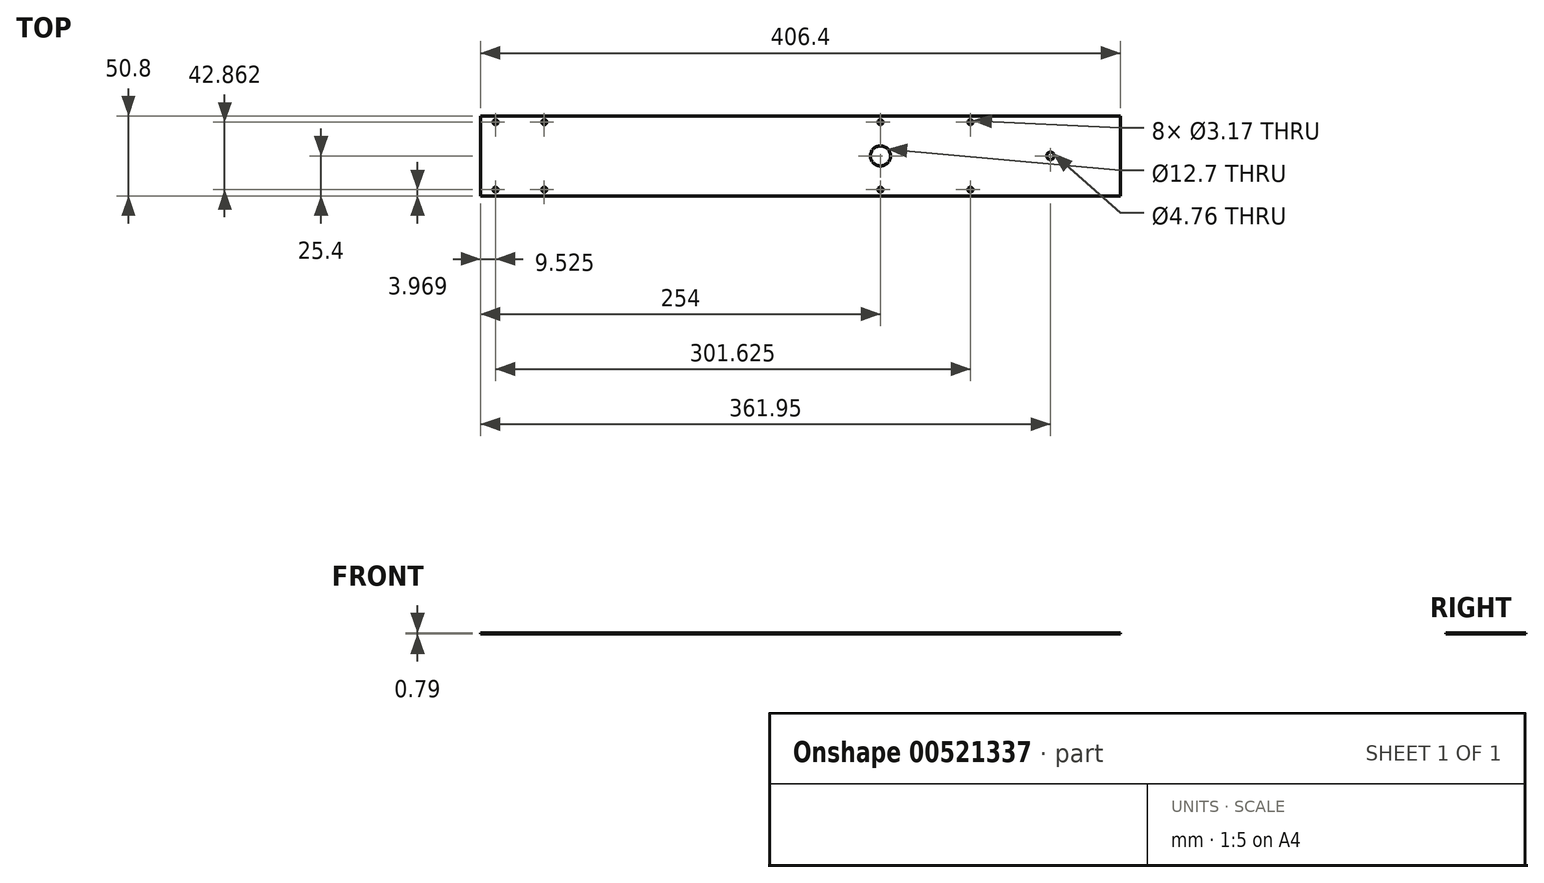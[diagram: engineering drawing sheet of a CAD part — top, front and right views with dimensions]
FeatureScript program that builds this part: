
annotation { "Feature Type Name" : "Feature", "Feature Type Description" : "" }
export const myFeature = defineFeature(function(context is Context, id is Id, definition is map)
    precondition{}
    {
        {
            var Q0;
            Q0=qCreatedBy(makeId("Top.planeOp"),FACE);
            var sketch = newSketch(context, id + "F0", { "sketchPlane" : qUnion([Q0])});
            skLineSegment(sketch, "E0.bottom", {"start": v(0, 0) * mm, "end": v(406.4, 0) * mm});
            skLineSegment(sketch, "E0.top", {"start": v(0, 50.8) * mm, "end": v(406.4, 50.8) * mm});
            skLineSegment(sketch, "E0.left", {"start": v(0, 0) * mm, "end": v(0, 50.8) * mm});
            skLineSegment(sketch, "E0.right", {"start": v(406.4, 0) * mm, "end": v(406.4, 50.8) * mm});
            skLineSegment(sketch, "E1", {"start": v(0, 25.4) * mm, "end": v(406.4, 25.4) * mm, "construction": true});
            skCircle(sketch, "E2", {"center": v(361.95, 25.4) * mm, "radius": 2.38 * mm});
            skCircle(sketch, "E3", {"center": v(254, 25.4) * mm, "radius": 6.35 * mm});
            skCircle(sketch, "E4", {"center": v(254, 46.83) * mm, "radius": 1.59 * mm});
            skCircle(sketch, "E5", {"center": v(311.15, 46.83) * mm, "radius": 1.59 * mm});
            skCircle(sketch, "E6", {"center": v(40.48, 46.83) * mm, "radius": 1.59 * mm});
            skCircle(sketch, "E7", {"center": v(9.53, 46.83) * mm, "radius": 1.59 * mm});
            skCircle(sketch, "E8.MirrorC", {"center": v(40.48, 3.97) * mm, "radius": 1.59 * mm});
            skCircle(sketch, "E9.MirrorC", {"center": v(9.53, 3.97) * mm, "radius": 1.59 * mm});
            skCircle(sketch, "E10.MirrorC", {"center": v(254, 3.97) * mm, "radius": 1.59 * mm});
            skCircle(sketch, "E11.MirrorC", {"center": v(311.15, 3.97) * mm, "radius": 1.59 * mm});
            skSolve(sketch);
        }
        {
            var Q0;
            Q0=makeQuery(id+"F0.imprint","IMPRINT",FACE,{"disambiguationData":[TD([[makeQuery(id+"F0.imprint","IMPRINT",EDGE,{"derivedFrom":sQuery(id+"F0.wireOp",EDGE,"E0.bottom")}),1.0]])]});
            extrude(context, id + "F1", {"entities" : qUnion([Q0]), "depth" : 0.8 * mm, "offsetDistance" : 25.4 * mm});
        }
    });
